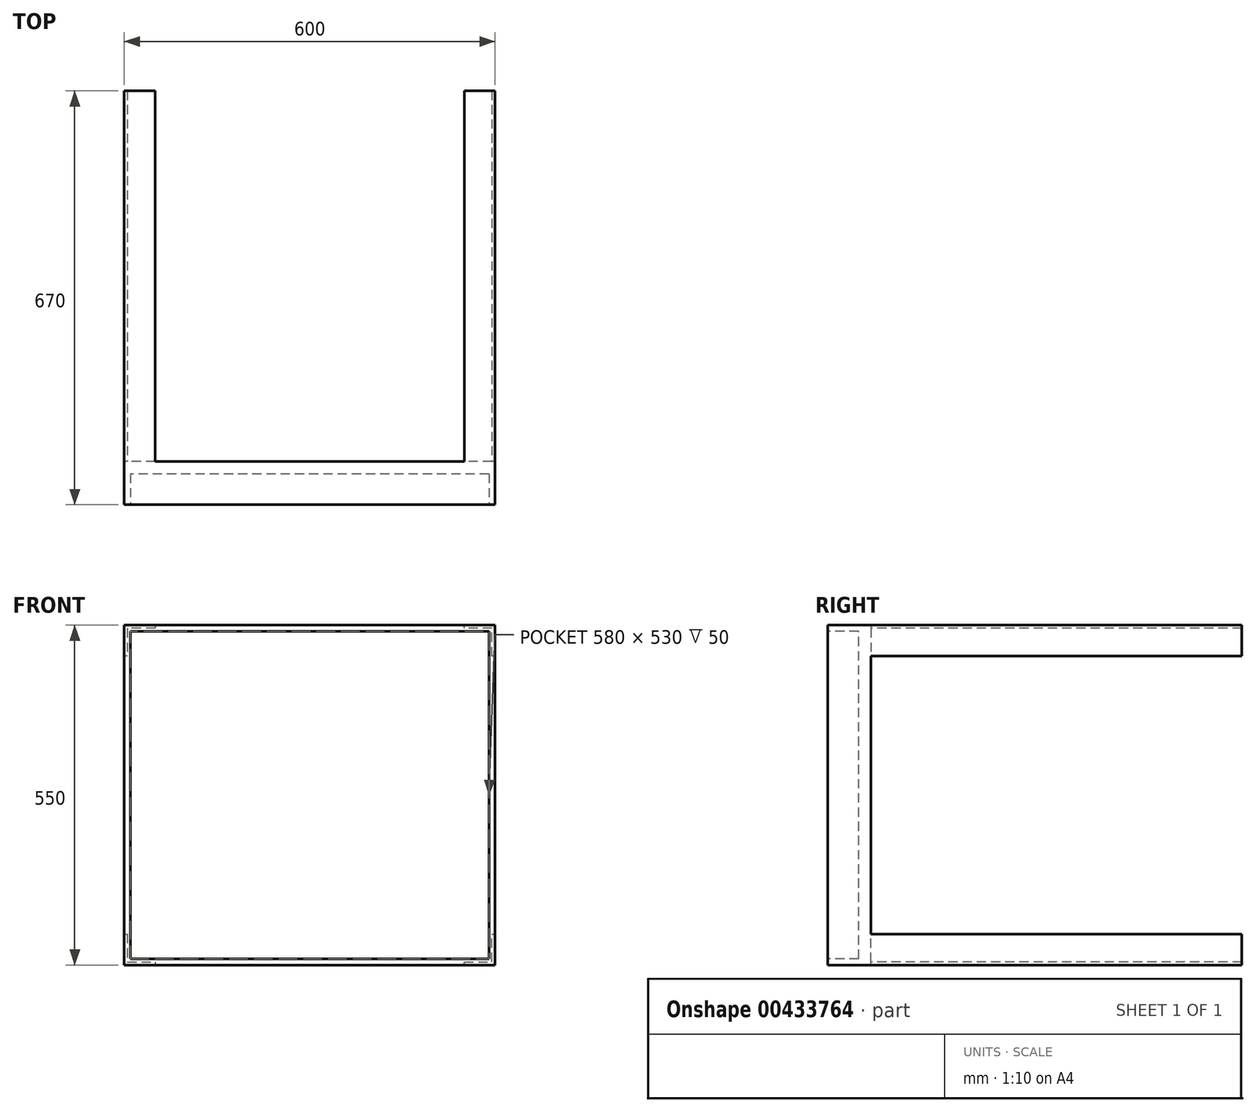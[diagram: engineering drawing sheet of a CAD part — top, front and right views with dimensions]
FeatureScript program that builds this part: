
annotation { "Feature Type Name" : "Feature", "Feature Type Description" : "" }
export const myFeature = defineFeature(function(context is Context, id is Id, definition is map)
    precondition{}
    {
        {
            var Q0;
            Q0=qCreatedBy(makeId("Front.planeOp"),FACE);
            var sketch = newSketch(context, id + "F0", { "sketchPlane" : qUnion([Q0])});
            skLineSegment(sketch, "E0.bottom", {"start": v(300, -275) * mm, "end": v(-300, -275) * mm});
            skLineSegment(sketch, "E0.top", {"start": v(300, 275) * mm, "end": v(-300, 275) * mm});
            skLineSegment(sketch, "E0.left", {"start": v(300, -275) * mm, "end": v(300, 275) * mm});
            skLineSegment(sketch, "E0.right", {"start": v(-300, -275) * mm, "end": v(-300, 275) * mm});
            skPoint(sketch, "E0.middle", {"position": v(0, 0) * mm});
            skSolve(sketch);
        }
        {
            var Q0;
            Q0=makeQuery(id+"F0.imprint","IMPRINT",FACE,{"disambiguationData":[TD([[makeQuery(id+"F0.imprint","IMPRINT",EDGE,{"derivedFrom":sQuery(id+"F0.wireOp",EDGE,"E0.bottom")}),-1.0]])]});
            extrude(context, id + "F1", {"entities" : qUnion([Q0]), "endBound" : BoundingType.SYMMETRIC, "depth" : 70 * mm});
        }
        {
            var Q0;
            Q0=makeQuery(id+"F1.opExtrude","CAP_FACE",FACE,{"disambiguationData":[OSD([sQuery(id+"F0.wireOp",EDGE,"E0.bottom"),sQuery(id+"F0.wireOp",EDGE,"E0.top"),sQuery(id+"F0.wireOp",EDGE,"E0.left"),sQuery(id+"F0.wireOp",EDGE,"E0.right")])],"isStart":true});
            var sketch = newSketch(context, id + "F2", { "sketchPlane" : qUnion([Q0])});
            skLineSegment(sketch, "E1", {"start": v(300, -275) * mm, "end": v(300, -225) * mm});
            skLineSegment(sketch, "E2", {"start": v(300, -275) * mm, "end": v(250, -275) * mm});
            skLineSegment(sketch, "E3", {"start": v(300, -225) * mm, "end": v(295, -225) * mm});
            skLineSegment(sketch, "E4", {"start": v(295, -225) * mm, "end": v(295, -270) * mm});
            skLineSegment(sketch, "E5", {"start": v(295, -270) * mm, "end": v(250, -270) * mm});
            skLineSegment(sketch, "E6", {"start": v(250, -270) * mm, "end": v(250, -275) * mm});
            skLineSegment(sketch, "E7", {"start": v(-300, -275) * mm, "end": v(-250, -275) * mm});
            skLineSegment(sketch, "E8", {"start": v(-300, -275) * mm, "end": v(-300, -225) * mm});
            skLineSegment(sketch, "E9", {"start": v(-250, -275) * mm, "end": v(-250, -270) * mm});
            skLineSegment(sketch, "E10", {"start": v(-250, -270) * mm, "end": v(-295, -270) * mm});
            skLineSegment(sketch, "E11", {"start": v(-295, -270) * mm, "end": v(-295, -225) * mm});
            skLineSegment(sketch, "E12", {"start": v(-295, -225) * mm, "end": v(-300, -225) * mm});
            skLineSegment(sketch, "E13", {"start": v(-300, 275) * mm, "end": v(-300, 225) * mm});
            skLineSegment(sketch, "E14", {"start": v(-300, 275) * mm, "end": v(-250, 275) * mm});
            skLineSegment(sketch, "E15", {"start": v(-300, 225) * mm, "end": v(-295, 225) * mm});
            skLineSegment(sketch, "E16", {"start": v(-295, 225) * mm, "end": v(-295, 270) * mm});
            skLineSegment(sketch, "E17", {"start": v(-295, 270) * mm, "end": v(-250, 270) * mm});
            skLineSegment(sketch, "E18", {"start": v(-250, 270) * mm, "end": v(-250, 275) * mm});
            skLineSegment(sketch, "E19", {"start": v(300, 275) * mm, "end": v(250, 275) * mm});
            skLineSegment(sketch, "E20", {"start": v(300, 275) * mm, "end": v(300, 225) * mm});
            skLineSegment(sketch, "E21", {"start": v(250, 275) * mm, "end": v(250, 270) * mm});
            skLineSegment(sketch, "E22", {"start": v(250, 270) * mm, "end": v(295, 270) * mm});
            skLineSegment(sketch, "E23", {"start": v(295, 270) * mm, "end": v(295, 225) * mm});
            skLineSegment(sketch, "E24", {"start": v(295, 225) * mm, "end": v(300, 225) * mm});
            skSolve(sketch);
        }
        {
            var Q0;
            Q0=makeQuery(id+"F2.imprint","IMPRINT",FACE,{"disambiguationData":[TD([[makeQuery(id+"F2.imprint","IMPRINT",EDGE,{"derivedFrom":sQuery(id+"F2.wireOp",EDGE,"E1")}),1.0]])]});
            var Q1;
            Q1=makeQuery(id+"F2.imprint","IMPRINT",FACE,{"disambiguationData":[TD([[makeQuery(id+"F2.imprint","IMPRINT",EDGE,{"derivedFrom":sQuery(id+"F2.wireOp",EDGE,"E7")}),1.0]])]});
            var Q2;
            Q2=makeQuery(id+"F2.imprint","IMPRINT",FACE,{"disambiguationData":[TD([[makeQuery(id+"F2.imprint","IMPRINT",EDGE,{"derivedFrom":sQuery(id+"F2.wireOp",EDGE,"E13")}),-1.0]])]});
            var Q3;
            Q3=makeQuery(id+"F2.imprint","IMPRINT",FACE,{"disambiguationData":[TD([[makeQuery(id+"F2.imprint","IMPRINT",EDGE,{"derivedFrom":sQuery(id+"F2.wireOp",EDGE,"E19")}),-1.0]])]});
            extrude(context, id + "F3", {"entities" : qUnion([Q0, Q1, Q2, Q3]), "operationType" : NewBodyOperationType.ADD, "depth" : 600 * mm});
        }
        {
            var Q0;
            Q0=makeQuery(id+"F1.opExtrude","CAP_FACE",FACE,{"disambiguationData":[OSD([sQuery(id+"F0.wireOp",EDGE,"E0.bottom"),sQuery(id+"F0.wireOp",EDGE,"E0.top"),sQuery(id+"F0.wireOp",EDGE,"E0.left"),sQuery(id+"F0.wireOp",EDGE,"E0.right")])],"isStart":false});
            var sketch = newSketch(context, id + "F4", { "sketchPlane" : qUnion([Q0])});
            skLineSegment(sketch, "E25.bottom", {"start": v(290, -265) * mm, "end": v(-290, -265) * mm});
            skLineSegment(sketch, "E25.top", {"start": v(290, 265) * mm, "end": v(-290, 265) * mm});
            skLineSegment(sketch, "E25.left", {"start": v(290, -265) * mm, "end": v(290, 265) * mm});
            skLineSegment(sketch, "E25.right", {"start": v(-290, -265) * mm, "end": v(-290, 265) * mm});
            skPoint(sketch, "E25.middle", {"position": v(0, 0) * mm});
            skSolve(sketch);
        }
        {
            var Q0;
            Q0=makeQuery(id+"F4.imprint","IMPRINT",FACE,{"disambiguationData":[TD([[makeQuery(id+"F4.imprint","IMPRINT",EDGE,{"derivedFrom":sQuery(id+"F4.wireOp",EDGE,"E25.bottom")}),-1.0]])]});
            extrude(context, id + "F5", {"entities" : qUnion([Q0]), "operationType" : NewBodyOperationType.REMOVE, "oppositeDirection" : true, "depth" : 50 * mm});
        }
    });
